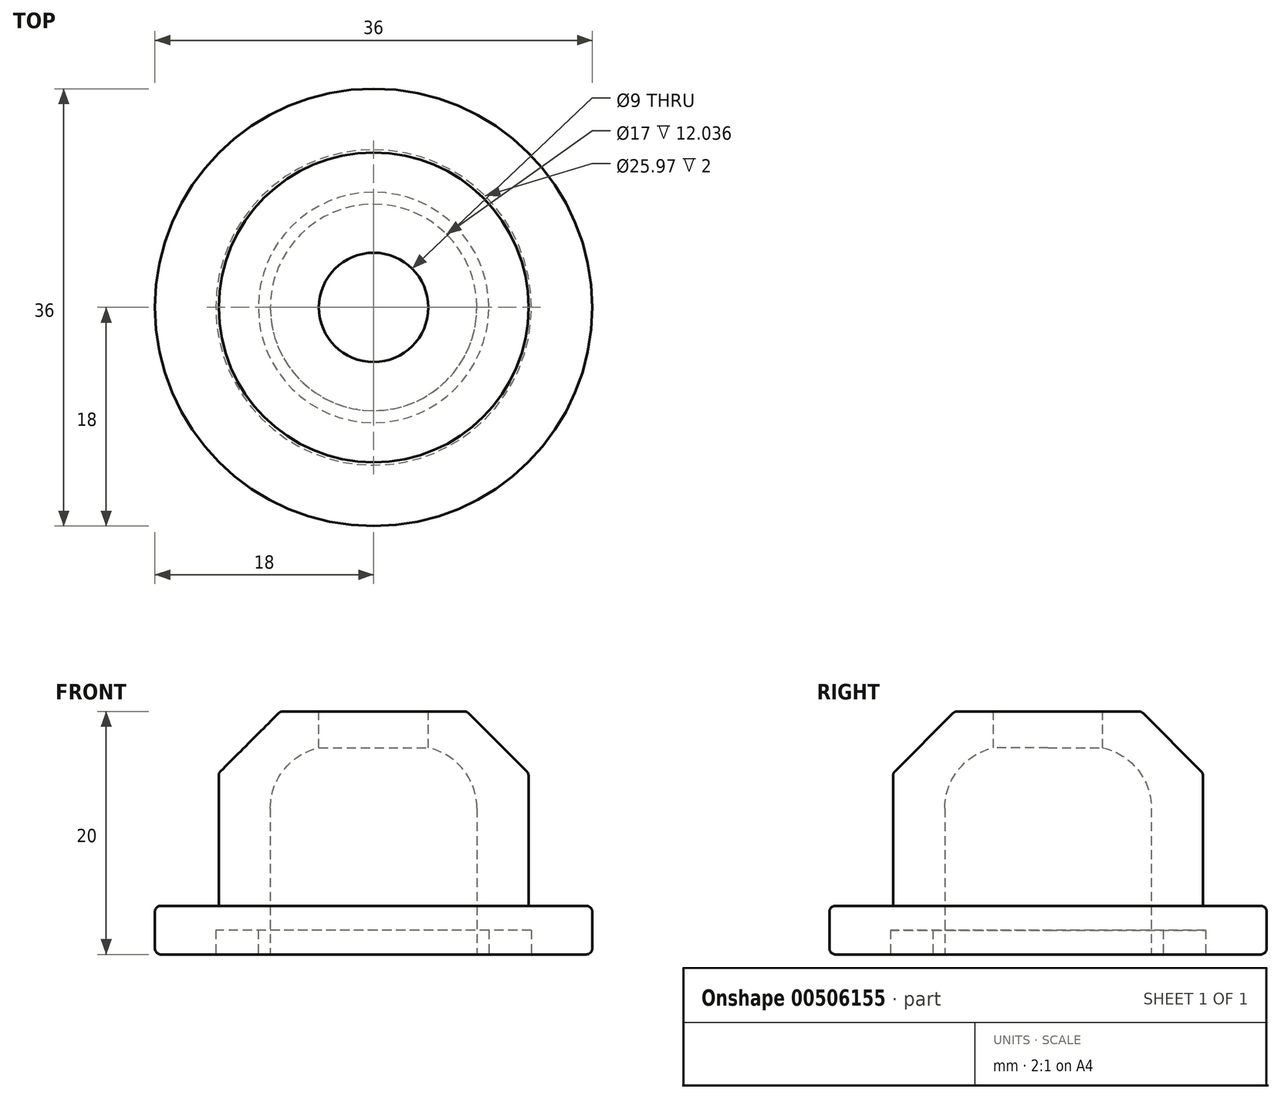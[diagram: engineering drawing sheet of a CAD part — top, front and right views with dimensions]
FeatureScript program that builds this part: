
annotation { "Feature Type Name" : "Feature", "Feature Type Description" : "" }
export const myFeature = defineFeature(function(context is Context, id is Id, definition is map)
    precondition{}
    {
        {
            var Q0;
            Q0=qCreatedBy(makeId("Top.planeOp"),FACE);
            var sketch = newSketch(context, id + "F0", { "sketchPlane" : qUnion([Q0])});
            skCircle(sketch, "E0", {"center": v(0, 0) * mm, "radius": 18 * mm});
            skSolve(sketch);
        }
        {
            var Q0;
            Q0 = qSketchRegion(id + "F0", true);
            extrude(context, id + "F1", {"entities" : qUnion([Q0]), "depth" : 4 * mm});
        }
        {
            var Q0;
            Q0=makeQuery(id+"F1.opExtrude","CAP_FACE",FACE,{"disambiguationData":[OSD([sQuery(id+"F0.wireOp",EDGE,"E0")])],"isStart":false});
            var sketch = newSketch(context, id + "F2", { "sketchPlane" : qUnion([Q0])});
            skCircle(sketch, "E1", {"center": v(0, 0) * mm, "radius": 12.75 * mm});
            skSolve(sketch);
        }
        {
            var Q0;
            Q0 = qSketchRegion(id + "F2", true);
            extrude(context, id + "F3", {"entities" : qUnion([Q0]), "operationType" : NewBodyOperationType.ADD, "depth" : 16 * mm});
        }
        {
            var Q0;
            Q0=makeQuery(id+"F3.opExtrude","CAP_FACE",FACE,{"disambiguationData":[OSD([sQuery(id+"F2.wireOp",EDGE,"E1")])],"isStart":false});
            var sketch = newSketch(context, id + "F4", { "sketchPlane" : qUnion([Q0])});
            skCircle(sketch, "E2", {"center": v(0, 0) * mm, "radius": 4.5 * mm});
            skSolve(sketch);
        }
        {
            var Q0;
            Q0 = qSketchRegion(id + "F4", true);
            extrude(context, id + "F5", {"entities" : qUnion([Q0]), "operationType" : NewBodyOperationType.REMOVE, "oppositeDirection" : true, "depth" : 21 * mm});
        }
        {
            var Q0;
            Q0=makeQuery(id+"F1.opExtrude","CAP_FACE",FACE,{"disambiguationData":[OSD([sQuery(id+"F0.wireOp",EDGE,"E0")])],"isStart":true});
            var sketch = newSketch(context, id + "F6", { "sketchPlane" : qUnion([Q0])});
            skCircle(sketch, "E3", {"center": v(0, 0) * mm, "radius": 8.5 * mm});
            skSolve(sketch);
        }
        {
            var Q0;
            Q0 = qSketchRegion(id + "F6", true);
            extrude(context, id + "F7", {"entities" : qUnion([Q0]), "operationType" : NewBodyOperationType.REMOVE, "oppositeDirection" : true, "depth" : 17 * mm});
        }
        {
            var Q0;
            Q0=makeQuery(id+"F1.opExtrude","CAP_FACE",FACE,{"disambiguationData":[OSD([sQuery(id+"F0.wireOp",EDGE,"E0")])],"isStart":true});
            var sketch = newSketch(context, id + "F8", { "sketchPlane" : qUnion([Q0])});
            skCircle(sketch, "E4", {"center": v(0, 0) * mm, "radius": 9.5 * mm});
            skSolve(sketch);
        }
        {
            var Q0;
            Q0=makeQuery(id+"F8.imprint","IMPRINT",FACE,{"disambiguationData":[TD([[makeQuery(id+"F8.imprint","IMPRINT",EDGE,{"derivedFrom":sQuery(id+"F8.wireOp",EDGE,"E4")}),-1.0]])]});
            var sketch = newSketch(context, id + "F9", { "sketchPlane" : qUnion([Q0])});
            skLineSegment(sketch, "E5.bottom", {"start": v(0, 9.48) * mm, "end": v(-0.1, 9.48) * mm});
            skLineSegment(sketch, "E5.top", {"start": v(0, 12.98) * mm, "end": v(-0.1, 12.98) * mm});
            skLineSegment(sketch, "E5.left", {"start": v(0, 9.48) * mm, "end": v(0, 12.98) * mm});
            skLineSegment(sketch, "E5.right", {"start": v(-0.1, 9.48) * mm, "end": v(-0.1, 12.98) * mm});
            skSolve(sketch);
        }
        {
            var Q0;
            Q0=makeQuery(id+"F8.imprint","IMPRINT",FACE,{"disambiguationData":[TD([[makeQuery(id+"F8.imprint","IMPRINT",EDGE,{"derivedFrom":sQuery(id+"F8.wireOp",EDGE,"E4")}),-1.0]])]});
            var Q1;
            Q1=sQuery(id+"F9.wireOp",EDGE,"E5.left");
            var Q2;
            Q2=sQuery(id+"F9.wireOp",EDGE,"E5.right");
            var Q3;
            Q3=sQuery(id+"F8.wireOp",EDGE,"E4");
            revolve(context, id + "F10", {"bodyType" : ToolBodyType.SURFACE, "operationType" : NewBodyOperationType.REMOVE, "entities" : qUnion([Q0]), "surfaceEntities" : qUnion([Q1, Q2]), "axis" : qUnion([Q3]), "revolveType" : RevolveType.FULL, "oppositeDirection" : true});
        }
        {
            var Q0;
            Q0=makeQuery(id+"F10.opRevolve","SWEPT_FACE",FACE,{"disambiguationData":[OSD([sQuery(id+"F9.wireOp",EDGE,"E5.right")])]});
            extrude(context, id + "F11", {"entities" : qUnion([Q0]), "operationType" : NewBodyOperationType.REMOVE, "depth" : 2 * mm});
        }
        {
            var Q0;
            Q0=makeQuery(id+"F7.boolean.opBoolean","COPY",EDGE,{"derivedFrom":makeQuery(id+"F7.opExtrude","CAP_EDGE",EDGE,{"disambiguationData":[OSD([sQuery(id+"F6.wireOp",EDGE,"E3")])],"isStart":false})});
            fillet(context, id + "F12", {"entities" : qUnion([Q0]), "radius" : 5.08 * mm, "tangentPropagation" : true, "allowEdgeOverflow" : false});
        }
        {
            var Q0;
            Q0=makeQuery(id+"F3.opExtrude","CAP_EDGE",EDGE,{"disambiguationData":[OSD([sQuery(id+"F2.wireOp",EDGE,"E1")])],"isStart":false});
            chamfer(context, id + "F13", {"entities" : qUnion([Q0]), "width" : 5.08 * mm, "tangentPropagation" : true});
        }
        {
            var Q0;
            {var subQ0=sQuery(id+"F2.wireOp",EDGE,"E1");Q0=makeQuery(id+"F13.opChamfer","BLEND_EDGE",EDGE,{"blendedFrom":[makeQuery(id+"F3.opExtrude","CAP_EDGE",EDGE,{"disambiguationData":[OSD([subQ0])],"isStart":false}),makeQuery(id+"F3.opExtrude","SWEPT_FACE",FACE,{"disambiguationData":[OSD([subQ0])]})],"blendedInto":[makeQuery(id+"F3.opExtrude","SWEPT_FACE",FACE,{"disambiguationData":[OSD([subQ0])]})]});}
            var Q1;
            {var subQ0=sQuery(id+"F2.wireOp",EDGE,"E1");Q1=makeQuery(id+"F13.opChamfer","BLEND_EDGE",EDGE,{"blendedFrom":[makeQuery(id+"F3.opExtrude","CAP_EDGE",EDGE,{"disambiguationData":[OSD([subQ0])],"isStart":false}),makeQuery(id+"F3.opExtrude","CAP_FACE",FACE,{"disambiguationData":[OSD([subQ0])],"isStart":false})],"blendedInto":[makeQuery(id+"F3.opExtrude","CAP_FACE",FACE,{"disambiguationData":[OSD([subQ0])],"isStart":false})]});}
            var Q2;
            Q2=makeQuery(id+"F5.boolean.opBoolean","COPY",EDGE,{"derivedFrom":makeQuery(id+"F5.opExtrude","CAP_EDGE",EDGE,{"disambiguationData":[OSD([sQuery(id+"F4.wireOp",EDGE,"E2")])],"isStart":true})});
            var Q3;
            Q3=makeQuery(id+"F1.opExtrude","CAP_EDGE",EDGE,{"disambiguationData":[OSD([sQuery(id+"F0.wireOp",EDGE,"E0")])],"isStart":true});
            var Q4;
            Q4=makeQuery(id+"F1.opExtrude","CAP_EDGE",EDGE,{"disambiguationData":[OSD([sQuery(id+"F0.wireOp",EDGE,"E0")])],"isStart":false});
            var Q5;
            Q5=makeQuery(id+"F3.opExtrude","CAP_EDGE",EDGE,{"disambiguationData":[OSD([sQuery(id+"F2.wireOp",EDGE,"E1")])],"isStart":true});
            fillet(context, id + "F14", {"entities" : qUnion([Q0, Q1, Q2, Q3, Q4, Q5]), "radius" : 0.5 * mm, "tangentPropagation" : true, "allowEdgeOverflow" : false});
        }
    });
